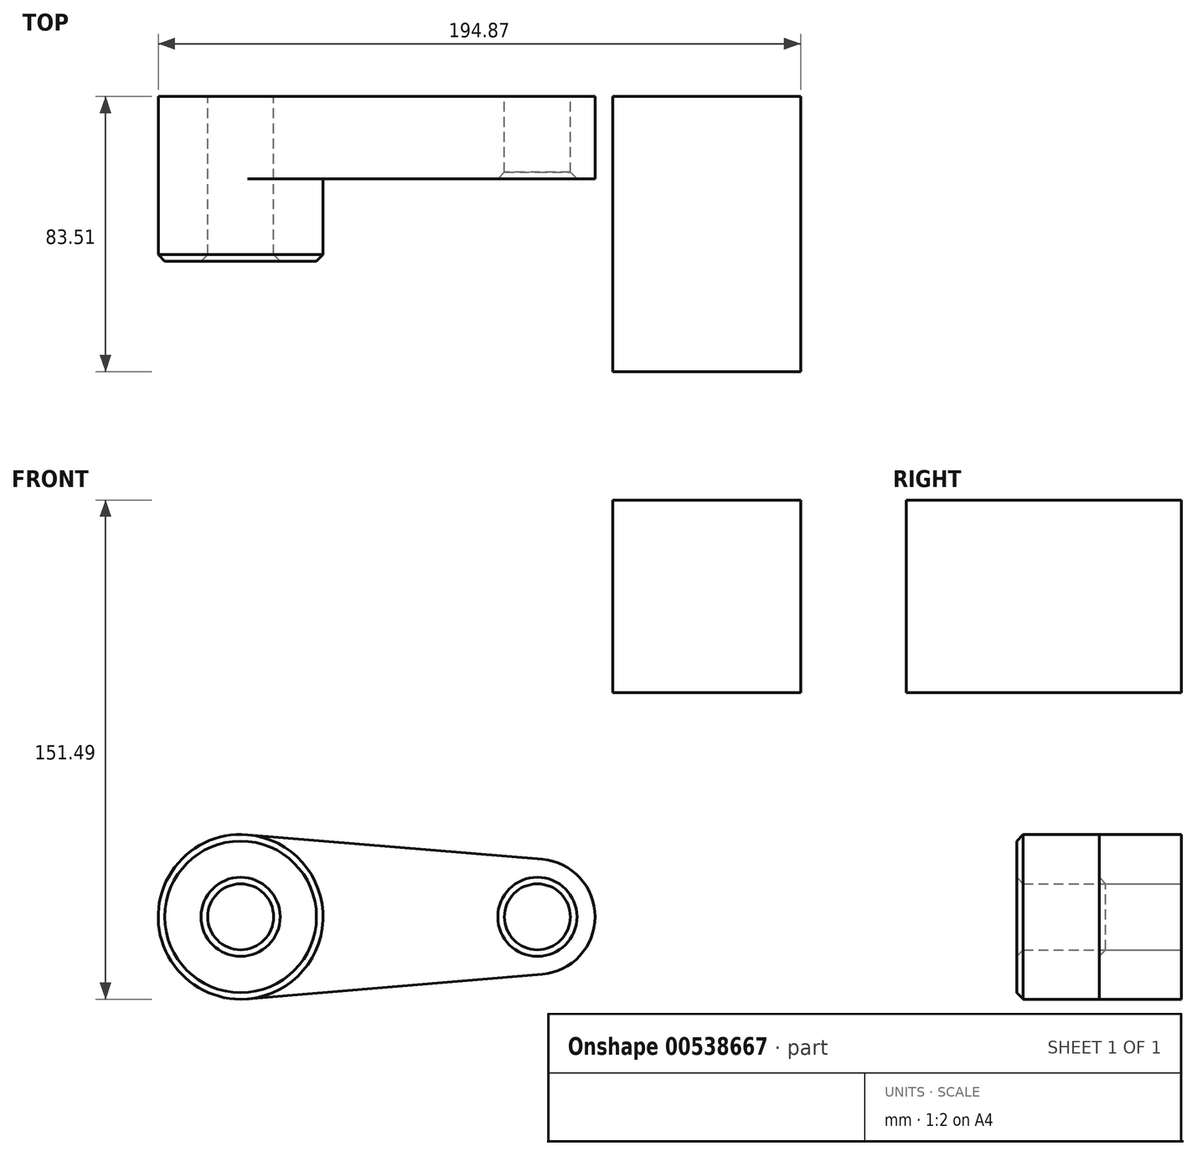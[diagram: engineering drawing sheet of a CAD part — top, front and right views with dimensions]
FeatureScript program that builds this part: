
annotation { "Feature Type Name" : "Feature", "Feature Type Description" : "" }
export const myFeature = defineFeature(function(context is Context, id is Id, definition is map)
    precondition{}
    {
        {
            var Q0;
            Q0=qCreatedBy(makeId("Front.planeOp"),FACE);
            var sketch = newSketch(context, id + "F0", { "sketchPlane" : qUnion([Q0])});
            skCircle(sketch, "E0", {"center": v(0, 0) * mm, "radius": 25 * mm});
            skCircle(sketch, "E1", {"center": v(90, 0) * mm, "radius": 17.5 * mm});
            skLineSegment(sketch, "E2", {"start": v(2.08, 24.91) * mm, "end": v(91.46, 17.44) * mm});
            skLineSegment(sketch, "E3", {"start": v(2.08, -24.91) * mm, "end": v(91.46, -17.44) * mm});
            skCircle(sketch, "E4", {"center": v(0, 0) * mm, "radius": 10 * mm});
            skCircle(sketch, "E5", {"center": v(90, 0) * mm, "radius": 10 * mm});
            skSolve(sketch);
        }
        {
            var Q0;
            Q0=qSketchRegion(id+"F0",true);
            extrude(context, id + "F1", {"entities" : qUnion([Q0]), "depth" : 25 * mm});
        }
        {
            var Q0;
            Q0=makeQuery(id+"F0.imprint","IMPRINT",FACE,{"disambiguationData":[TD([[makeQuery(id+"F0.imprint","IMPRINT",EDGE,{"derivedFrom":sQuery(id+"F0.wireOp",EDGE,"E4")}),-1.0]])]});
            extrude(context, id + "F2", {"entities" : qUnion([Q0]), "operationType" : NewBodyOperationType.ADD, "depth" : 50 * mm});
        }
        {
            var Q0;
            Q0=makeQuery(id+"F2.opExtrude","CAP_EDGE",EDGE,{"disambiguationData":[OSD([sQuery(id+"F0.wireOp",EDGE,"E0")])],"isStart":false});
            var Q1;
            Q1=makeQuery(id+"F2.opExtrude","CAP_EDGE",EDGE,{"disambiguationData":[OSD([sQuery(id+"F0.wireOp",EDGE,"E4")])],"isStart":false});
            var Q2;
            Q2=makeQuery(id+"F1.opExtrude","CAP_EDGE",EDGE,{"disambiguationData":[OSD([sQuery(id+"F0.wireOp",EDGE,"E5")])],"isStart":false});
            chamfer(context, id + "F3", {"entities" : qUnion([Q0, Q1, Q2]), "width" : 2 * mm, "tangentPropagation" : true});
        }
        {
            var Q0;
            Q0 = qSketchRegion(id + "F0", true);
            var sketch = newSketch(context, id + "F4", { "sketchPlane" : qUnion([Q0])});
            skLineSegment(sketch, "E6", {"start": v(169.87, 126.49) * mm, "end": v(169.87, 68.05) * mm});
            skLineSegment(sketch, "E7", {"start": v(169.87, 68.05) * mm, "end": v(112.88, 68.05) * mm});
            skLineSegment(sketch, "E8", {"start": v(112.88, 68.05) * mm, "end": v(112.88, 126.49) * mm});
            skLineSegment(sketch, "E9", {"start": v(112.88, 126.49) * mm, "end": v(169.87, 126.49) * mm});
            skSolve(sketch);
        }
        {
            var Q0;
            Q0 = qSketchRegion(id + "F4", true);
            extrude(context, id + "F5", {"entities" : qUnion([Q0]), "depth" : 83.51 * mm, "offsetDistance" : 25 * mm});
        }
    });
